# Revit family: NLRS_57_AIR_UN_ceiling-diffuser-rrbs_return_LT_sacs
name_source: partatom
category: Air Terminals
units: mm (PartAtom-declared; Revit-internal decimal feet)

## family parameters
Always vertical = Yes
Cut with Voids When Loaded = No
Part Type = Normal
Room Calculation Point = Yes
Round Connector Dimension = Use Diameter
Shared = No
Work Plane-Based = No

## types (3) — shared parameters
Assembly Code = 57.00
Description = Modular Swirl return grill, Type RRBS
Flip_Connector_to_left = No
IfcExportAs = IfcAirterminal
IfcExportType = Diffuser
Manufacturer = Solid Air Climate Solutions
Model = RRBS
NLRS_C_content_datum_uitgifte = 16-04-2024
NLRS_C_content_provider = Solid Air Climate Solutions
NLRS_C_content_versie = 3.21.04
NLRS_C_description = Modular Swirl return grill, Type RRBS
SACS_Arrow_Start = 325 mm  [stored 1.06627 ft]
SACS_Data_Hidden = RRBS_Data
SACS_DbA_Text = Db(A)
SACS_Plenum_Material = NLRS_57_sendzimir verzinkt_gen_sacs
Type Comments = Please make sure flow is set to m3/h!
URL = https://solid-air.nl
zero-valued in all types: Cost, Default Elevation

## per-type parameters (varying)
| type | Max Flow | Min Flow | SACS_Base_Index | SACS_Factor_LpF1 | SACS_Factor_LpF2 | SACS_Factor_PsF1 | SACS_Factor_PsF2 | SACS_Plenum_A | SACS_Plenum_D1 | SACS_Plenum_D2oval_H | SACS_Plenum_D2oval_W | SACS_Plenum_T |
| 250 | 80.0 L/s | 20.0 L/s | 1 | -107.199708 | 25.560764 | 0.000516 | 2.035595 | 303 mm  [stored 0.994094 ft] | 123 mm  [stored 0.403543 ft] | 73 mm  [stored 0.239501 ft] | 164 mm  [stored 0.538058 ft] | 60 mm  [stored 0.19685 ft] |
| 350 | 125.0 L/s | 30.0 L/s | 2 | -120.902454 | 25.726251 | 0.000219 | 2.003284 | 403 mm  [stored 1.32218 ft] | 158 mm | 93 mm  [stored 0.305118 ft] | 208 mm | 70 mm  [stored 0.229659 ft] |
| 450 | 200.0 L/s | 50.0 L/s | 3 | -135.437949 | 26.085877 | 7.2e-05 | 1.997425 | 503 mm  [stored 1.65026 ft] | 198 mm | 117 mm  [stored 0.383858 ft] | 262 mm  [stored 0.85958 ft] | 80 mm  [stored 0.262467 ft] |

note: [stored X ft] marks values corroborated as IEEE doubles in the binary element streams (Revit-internal decimal feet)

## geometry (parser evidence)
native form markers: Sweep x21
no freeform markers — native parametric forms only
